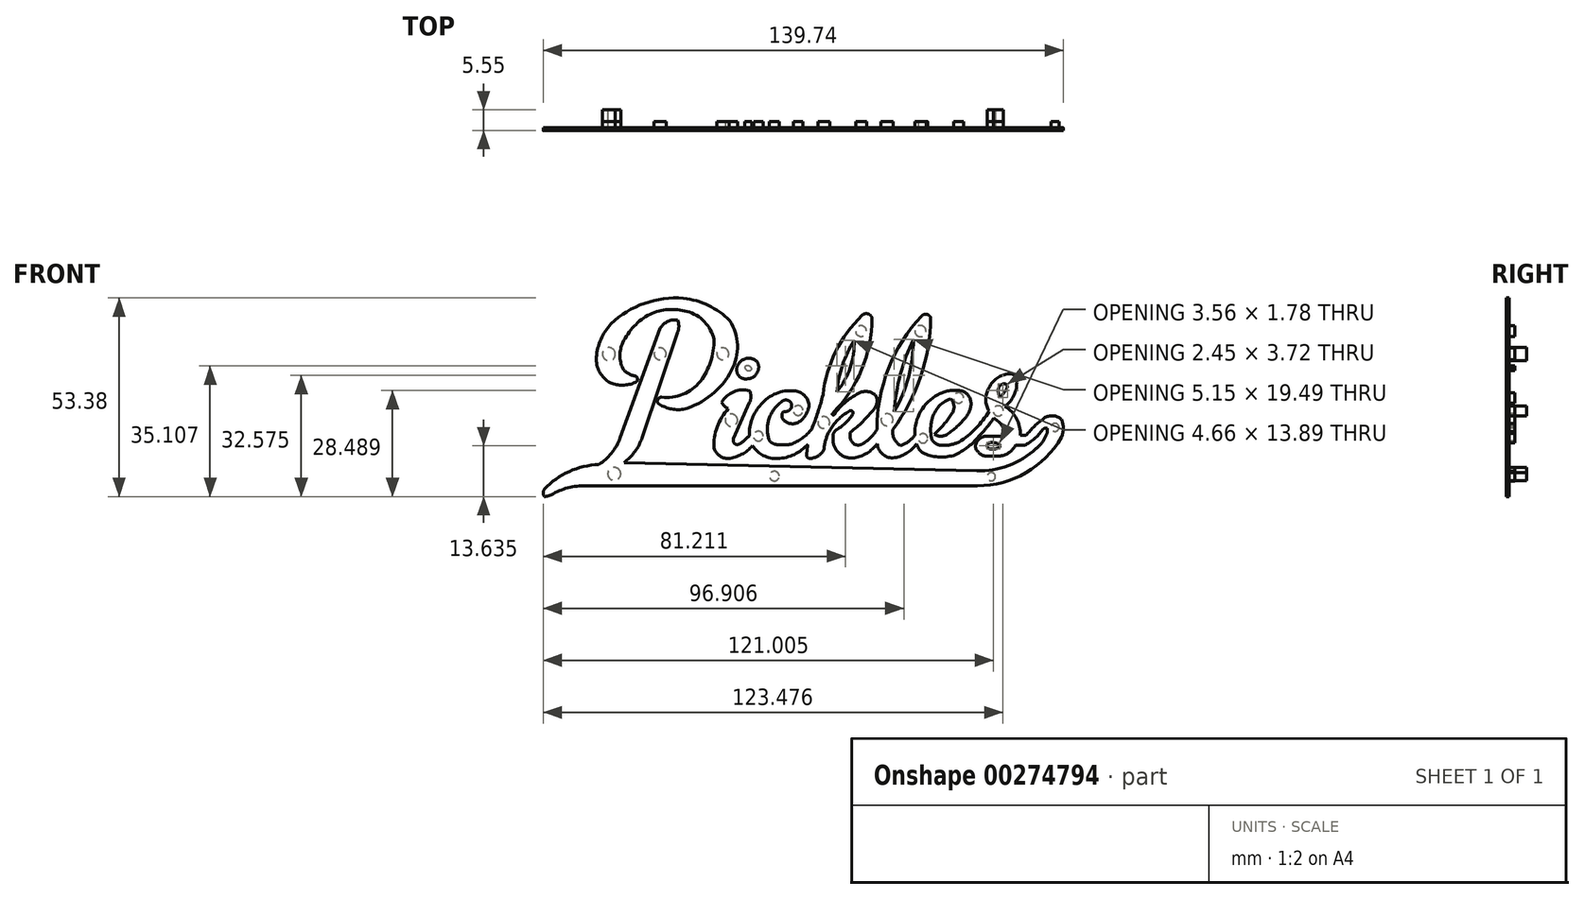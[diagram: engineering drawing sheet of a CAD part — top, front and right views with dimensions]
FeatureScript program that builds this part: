
annotation { "Feature Type Name" : "Feature", "Feature Type Description" : "" }
export const myFeature = defineFeature(function(context is Context, id is Id, definition is map)
    precondition{}
    {
        {
            var Q0;
            Q0=qCreatedBy(makeId("Front.planeOp"),FACE);
            var sketch = newSketch(context, id + "F0", { "sketchPlane" : qUnion([Q0])});
            skArc(sketch, "E0", {"start": v(-54.7, 9.9) * mm, "mid": v(-51.38, 9.32) * mm, "end": v(-48.08, 10.03) * mm});
            skArc(sketch, "E1", {"start": v(-58.51, 16.82) * mm, "mid": v(-57.6, 12.82) * mm, "end": v(-54.7, 9.9) * mm});
            skArc(sketch, "E2", {"start": v(-54.57, 25.8) * mm, "mid": v(-57.28, 21.63) * mm, "end": v(-58.51, 16.82) * mm});
            skArc(sketch, "E3", {"start": v(-35.11, 32.66) * mm, "mid": v(-45.57, 31.3) * mm, "end": v(-54.57, 25.8) * mm});
            skArc(sketch, "E4", {"start": v(-22.67, 26.65) * mm, "mid": v(-28.37, 30.74) * mm, "end": v(-35.11, 32.66) * mm});
            skArc(sketch, "E5", {"start": v(-22.17, 13.33) * mm, "mid": v(-20.58, 20.06) * mm, "end": v(-22.67, 26.65) * mm});
            skArc(sketch, "E6", {"start": v(-35.11, 2.8) * mm, "mid": v(-27.55, 6.72) * mm, "end": v(-22.17, 13.33) * mm});
            skArc(sketch, "E7", {"start": v(-41.96, 4.45) * mm, "mid": v(-38.7, 2.99) * mm, "end": v(-35.11, 2.8) * mm});
            skArc(sketch, "E8", {"start": v(-41.02, 6.1) * mm, "mid": v(-41.94, 5.53) * mm, "end": v(-41.96, 4.45) * mm});
            skArc(sketch, "E9", {"start": v(-41.02, 6.1) * mm, "mid": v(-35.23, 6.85) * mm, "end": v(-30.55, 10.33) * mm});
            skArc(sketch, "E10", {"start": v(-30.55, 10.33) * mm, "mid": v(-27.78, 15.65) * mm, "end": v(-26.9, 21.58) * mm});
            skArc(sketch, "E11", {"start": v(-26.9, 21.58) * mm, "mid": v(-29.46, 26.35) * mm, "end": v(-34.12, 29.13) * mm});
            skArc(sketch, "E12", {"start": v(-34.12, 29.13) * mm, "mid": v(-39.17, 29.63) * mm, "end": v(-44.1, 28.4) * mm});
            skArc(sketch, "E13", {"start": v(-44.1, 28.4) * mm, "mid": v(-48.36, 25.13) * mm, "end": v(-51.4, 20.71) * mm});
            skArc(sketch, "E14", {"start": v(-51.4, 20.71) * mm, "mid": v(-52.15, 17.27) * mm, "end": v(-51.4, 13.82) * mm});
            skArc(sketch, "E15", {"start": v(-51.4, 13.82) * mm, "mid": v(-49.9, 12.42) * mm, "end": v(-47.96, 11.76) * mm});
            skArc(sketch, "E16", {"start": v(-48.08, 10.03) * mm, "mid": v(-47.4, 10.85) * mm, "end": v(-47.96, 11.76) * mm});
            skArc(sketch, "E17", {"start": v(-36.65, 26.8) * mm, "mid": v(-39.31, 26.43) * mm, "end": v(-41.3, 24.63) * mm});
            skArc(sketch, "E18", {"start": v(-36.65, 23.5) * mm, "mid": v(-36.33, 25.15) * mm, "end": v(-36.65, 26.8) * mm});
            skLineSegment(sketch, "E19", {"start": v(-41.3, 24.63) * mm, "end": v(-52.12, -4.9) * mm});
            skLineSegment(sketch, "E20", {"start": v(-36.65, 23.5) * mm, "end": v(-46.17, -4.75) * mm});
            skArc(sketch, "E21", {"start": v(-51.06, -11.47) * mm, "mid": v(-48.1, -8.49) * mm, "end": v(-46.17, -4.75) * mm});
            skArc(sketch, "E22", {"start": v(-57.84, -12.05) * mm, "mid": v(-54.4, -8.95) * mm, "end": v(-52.12, -4.9) * mm});
            skArc(sketch, "E23", {"start": v(-57.84, -12.05) * mm, "mid": v(-65.8, -13.88) * mm, "end": v(-72.41, -18.66) * mm});
            skArc(sketch, "E24", {"start": v(-61.3, -17.73) * mm, "mid": v(-66.12, -18.3) * mm, "end": v(-70.6, -20.15) * mm});
            skArc(sketch, "E25", {"start": v(-72.41, -20.64) * mm, "mid": v(-71.49, -20.48) * mm, "end": v(-70.6, -20.15) * mm});
            skArc(sketch, "E26", {"start": v(-72.41, -18.66) * mm, "mid": v(-72.78, -19.65) * mm, "end": v(-72.41, -20.64) * mm});
            skLineSegment(sketch, "E27", {"start": v(-61.3, -17.73) * mm, "end": v(43.85, -17.73) * mm});
            skLineSegment(sketch, "E28", {"start": v(-51.06, -11.47) * mm, "end": v(43.72, -13.74) * mm});
            skArc(sketch, "E29", {"start": v(43.72, -13.74) * mm, "mid": v(52.27, -12.29) * mm, "end": v(59.66, -7.75) * mm});
            skArc(sketch, "E30", {"start": v(43.85, -17.73) * mm, "mid": v(56.9, -14.23) * mm, "end": v(66.45, -4.67) * mm});
            skArc(sketch, "E31", {"start": v(59.66, -7.75) * mm, "mid": v(61.3, -6.08) * mm, "end": v(62.43, -4.04) * mm});
            skArc(sketch, "E32", {"start": v(62.43, -4.04) * mm, "mid": v(62.67, -3.16) * mm, "end": v(62.69, -2.25) * mm});
            skArc(sketch, "E33", {"start": v(62.69, -2.25) * mm, "mid": v(61.98, -2.3) * mm, "end": v(61.38, -2.69) * mm});
            skArc(sketch, "E34", {"start": v(56.53, -6.87) * mm, "mid": v(59.22, -5.08) * mm, "end": v(61.38, -2.69) * mm});
            skLineSegment(sketch, "E35", {"start": v(56.53, -6.87) * mm, "end": v(54.08, -6.87) * mm});
            skArc(sketch, "E36", {"start": v(66.45, -4.67) * mm, "mid": v(66.96, -2.28) * mm, "end": v(66.45, 0.12) * mm});
            skArc(sketch, "E37", {"start": v(61.8, 0.47) * mm, "mid": v(59.22, -1.72) * mm, "end": v(56.95, -4.21) * mm});
            skArc(sketch, "E38", {"start": v(66.45, 0.12) * mm, "mid": v(64.18, 1.08) * mm, "end": v(61.8, 0.47) * mm});
            skLineSegment(sketch, "E39", {"start": v(56.95, -4.21) * mm, "end": v(55.36, -4.21) * mm});
            skArc(sketch, "E40", {"start": v(49.68, -9.75) * mm, "mid": v(52.27, -8.9) * mm, "end": v(54.08, -6.87) * mm});
            skLineSegment(sketch, "E41", {"start": v(49.68, -9.75) * mm, "end": v(46.47, -9.75) * mm});
            skArc(sketch, "E42", {"start": v(43.35, -7.37) * mm, "mid": v(44.5, -9.09) * mm, "end": v(46.47, -9.75) * mm});
            skArc(sketch, "E43", {"start": v(45.81, -4.46) * mm, "mid": v(44.06, -5.48) * mm, "end": v(43.35, -7.37) * mm});
            skLineSegment(sketch, "E44", {"start": v(45.81, -4.46) * mm, "end": v(51.38, -4.46) * mm});
            skArc(sketch, "E45", {"start": v(51.38, -4.46) * mm, "mid": v(50.5, -1.59) * mm, "end": v(48.25, 0.42) * mm});
            skArc(sketch, "E46", {"start": v(44.66, -4.02) * mm, "mid": v(46.55, -1.88) * mm, "end": v(48.25, 0.42) * mm});
            skArc(sketch, "E47", {"start": v(37.45, -9.59) * mm, "mid": v(41.4, -7.25) * mm, "end": v(44.66, -4.02) * mm});
            skArc(sketch, "E48", {"start": v(29.2, -8.89) * mm, "mid": v(33.27, -9.96) * mm, "end": v(37.45, -9.59) * mm});
            skArc(sketch, "E49", {"start": v(27.57, -6.47) * mm, "mid": v(28.15, -7.84) * mm, "end": v(29.2, -8.89) * mm});
            skArc(sketch, "E50", {"start": v(55.36, -4.21) * mm, "mid": v(54.42, 0.29) * mm, "end": v(51.25, 3.61) * mm});
            skArc(sketch, "E51", {"start": v(51.25, 3.61) * mm, "mid": v(53.88, 6.97) * mm, "end": v(54.36, 11.2) * mm});
            skArc(sketch, "E52", {"start": v(54.36, 11.2) * mm, "mid": v(53.55, 12.11) * mm, "end": v(52.36, 12.35) * mm});
            skArc(sketch, "E53", {"start": v(52.36, 12.35) * mm, "mid": v(49.2, 11.21) * mm, "end": v(47.04, 8.65) * mm});
            skArc(sketch, "E54", {"start": v(47.04, 8.65) * mm, "mid": v(46.15, 5.48) * mm, "end": v(47.04, 2.3) * mm});
            skArc(sketch, "E55", {"start": v(39, -5.95) * mm, "mid": v(43.48, -2.28) * mm, "end": v(47.04, 2.3) * mm});
            skArc(sketch, "E56", {"start": v(36.7, 5.63) * mm, "mid": v(33.26, 3.28) * mm, "end": v(31.53, -0.51) * mm});
            skArc(sketch, "E57", {"start": v(37.05, 1.64) * mm, "mid": v(37.6, 3.7) * mm, "end": v(36.7, 5.63) * mm});
            skArc(sketch, "E58", {"start": v(32.32, -3.88) * mm, "mid": v(34.86, -1.27) * mm, "end": v(37.05, 1.64) * mm});
            skArc(sketch, "E59", {"start": v(32.32, -3.88) * mm, "mid": v(34.03, -4.42) * mm, "end": v(35.73, -3.88) * mm});
            skArc(sketch, "E60", {"start": v(35.73, -3.88) * mm, "mid": v(38.45, -1.81) * mm, "end": v(40.77, 0.7) * mm});
            skArc(sketch, "E61", {"start": v(40.77, 0.7) * mm, "mid": v(41.76, 2.35) * mm, "end": v(42.16, 4.23) * mm});
            skArc(sketch, "E62", {"start": v(42.16, 4.23) * mm, "mid": v(41.45, 6.52) * mm, "end": v(39.42, 7.8) * mm});
            skArc(sketch, "E63", {"start": v(39.42, 7.8) * mm, "mid": v(36.29, 7.8) * mm, "end": v(33.33, 6.8) * mm});
            skArc(sketch, "E64", {"start": v(33.33, 6.8) * mm, "mid": v(28.64, 2.26) * mm, "end": v(27.1, -4.08) * mm});
            skArc(sketch, "E65", {"start": v(23.2, -6.91) * mm, "mid": v(25.38, -5.81) * mm, "end": v(27.1, -4.08) * mm});
            skArc(sketch, "E66", {"start": v(21.15, -2.6) * mm, "mid": v(21.5, -5.07) * mm, "end": v(23.2, -6.91) * mm});
            skArc(sketch, "E67", {"start": v(21.15, -2.6) * mm, "mid": v(28.64, 11.64) * mm, "end": v(31.33, 27.5) * mm});
            skArc(sketch, "E68", {"start": v(31.33, 27.5) * mm, "mid": v(30.2, 28.35) * mm, "end": v(28.85, 27.9) * mm});
            skArc(sketch, "E69", {"start": v(28.85, 27.9) * mm, "mid": v(19.98, 13.78) * mm, "end": v(16.93, -2.6) * mm});
            skArc(sketch, "E70", {"start": v(21.15, -10.26) * mm, "mid": v(24.76, -9.04) * mm, "end": v(27.57, -6.47) * mm});
            skArc(sketch, "E71", {"start": v(16.93, -6.47) * mm, "mid": v(18.33, -9.15) * mm, "end": v(21.15, -10.26) * mm});
            skArc(sketch, "E72", {"start": v(10.8, -10.26) * mm, "mid": v(14.22, -8.94) * mm, "end": v(16.93, -6.47) * mm});
            skArc(sketch, "E73", {"start": v(5.1, -4.74) * mm, "mid": v(6.61, -8.87) * mm, "end": v(10.8, -10.26) * mm});
            skArc(sketch, "E74", {"start": v(6.18, -2.6) * mm, "mid": v(5.3, -3.5) * mm, "end": v(5.1, -4.74) * mm});
            skArc(sketch, "E75", {"start": v(6.18, -2.6) * mm, "mid": v(8.55, -0.76) * mm, "end": v(10.45, 1.57) * mm});
            skArc(sketch, "E76", {"start": v(9.45, 2.36) * mm, "mid": v(6.38, -0.02) * mm, "end": v(4.05, -3.13) * mm});
            skArc(sketch, "E77", {"start": v(10.45, 1.57) * mm, "mid": v(10.23, 2.33) * mm, "end": v(9.45, 2.36) * mm});
            skArc(sketch, "E78", {"start": v(4.05, -3.13) * mm, "mid": v(3.08, -5.55) * mm, "end": v(2.62, -8.12) * mm});
            skArc(sketch, "E79", {"start": v(-1.14, -10.4) * mm, "mid": v(1.02, -9.72) * mm, "end": v(2.62, -8.12) * mm});
            skArc(sketch, "E80", {"start": v(-2.03, -9.47) * mm, "mid": v(-1.78, -10.12) * mm, "end": v(-1.14, -10.4) * mm});
            skArc(sketch, "E81", {"start": v(-1.66, -6.54) * mm, "mid": v(-1.86, -8) * mm, "end": v(-2.03, -9.47) * mm});
            skArc(sketch, "E82", {"start": v(-9.76, -10.4) * mm, "mid": v(-5.3, -9.31) * mm, "end": v(-1.66, -6.54) * mm});
            skArc(sketch, "E83", {"start": v(-16.54, -6.96) * mm, "mid": v(-13.62, -9.6) * mm, "end": v(-9.76, -10.4) * mm});
            skArc(sketch, "E84", {"start": v(-23.03, -10.4) * mm, "mid": v(-19.46, -9.3) * mm, "end": v(-16.54, -6.96) * mm});
            skArc(sketch, "E85", {"start": v(-26.84, -7.62) * mm, "mid": v(-25.42, -9.68) * mm, "end": v(-23.03, -10.4) * mm});
            skArc(sketch, "E86", {"start": v(-23.03, 3.02) * mm, "mid": v(-26.05, -1.9) * mm, "end": v(-26.84, -7.62) * mm});
            skArc(sketch, "E87", {"start": v(-24.83, 4.7) * mm, "mid": v(-24.09, 3.69) * mm, "end": v(-23.03, 3.02) * mm});
            skArc(sketch, "E88", {"start": v(-17.32, 7.82) * mm, "mid": v(-21.6, 7.53) * mm, "end": v(-24.83, 4.7) * mm});
            skArc(sketch, "E89", {"start": v(-17.32, 4.7) * mm, "mid": v(-16.97, 6.26) * mm, "end": v(-17.32, 7.82) * mm});
            skLineSegment(sketch, "E90", {"start": v(-17.32, 4.7) * mm, "end": v(-21.64, -5.1) * mm});
            skArc(sketch, "E91", {"start": v(-21.64, -5.1) * mm, "mid": v(-21.3, -6.44) * mm, "end": v(-19.9, -6.4) * mm});
            skArc(sketch, "E92", {"start": v(-19.9, -6.4) * mm, "mid": v(-18.59, -5.38) * mm, "end": v(-17.38, -4.24) * mm});
            skArc(sketch, "E93", {"start": v(-14.2, 4.17) * mm, "mid": v(-16.63, 0.28) * mm, "end": v(-17.38, -4.24) * mm});
            skArc(sketch, "E94", {"start": v(-5.33, 7.78) * mm, "mid": v(-10.2, 7.07) * mm, "end": v(-14.2, 4.17) * mm});
            skArc(sketch, "E95", {"start": v(-1.33, 3.86) * mm, "mid": v(-2.6, 6.57) * mm, "end": v(-5.33, 7.78) * mm});
            skArc(sketch, "E96", {"start": v(-4.28, -0.71) * mm, "mid": v(-2.3, 1.24) * mm, "end": v(-1.33, 3.86) * mm});
            skArc(sketch, "E97", {"start": v(-8.27, 0.02) * mm, "mid": v(-6.4, -1) * mm, "end": v(-4.28, -0.71) * mm});
            skArc(sketch, "E98", {"start": v(-8.27, 2.23) * mm, "mid": v(-8.62, 1.13) * mm, "end": v(-8.27, 0.02) * mm});
            skArc(sketch, "E99", {"start": v(-8.27, 2.23) * mm, "mid": v(-7.13, 2.31) * mm, "end": v(-6.22, 3) * mm});
            skArc(sketch, "E100", {"start": v(-6.22, 3) * mm, "mid": v(-6.1, 4.35) * mm, "end": v(-7.1, 5.26) * mm});
            skArc(sketch, "E101", {"start": v(-7.1, 5.26) * mm, "mid": v(-7.87, 5.3) * mm, "end": v(-8.6, 5.02) * mm});
            skArc(sketch, "E102", {"start": v(-8.6, 5.02) * mm, "mid": v(-10.73, 2.84) * mm, "end": v(-12.18, 0.16) * mm});
            skArc(sketch, "E103", {"start": v(-12.18, 0.16) * mm, "mid": v(-12.52, -2.51) * mm, "end": v(-12.18, -5.18) * mm});
            skArc(sketch, "E104", {"start": v(-12.18, -5.18) * mm, "mid": v(-11.5, -6.08) * mm, "end": v(-10.5, -6.56) * mm});
            skArc(sketch, "E105", {"start": v(-10.5, -6.56) * mm, "mid": v(-8.37, -6.75) * mm, "end": v(-6.24, -6.56) * mm});
            skArc(sketch, "E106", {"start": v(-6.24, -6.56) * mm, "mid": v(-3.17, -4.93) * mm, "end": v(-0.66, -2.53) * mm});
            skArc(sketch, "E107", {"start": v(-0.66, -2.53) * mm, "mid": v(1.04, 2.05) * mm, "end": v(2.4, 6.75) * mm});
            skArc(sketch, "E108", {"start": v(12.88, 28.08) * mm, "mid": v(5.8, 18.31) * mm, "end": v(2.4, 6.75) * mm});
            skArc(sketch, "E109", {"start": v(15.58, 27.28) * mm, "mid": v(14.47, 28.49) * mm, "end": v(12.88, 28.08) * mm});
            skArc(sketch, "E110", {"start": v(4.96, 1.73) * mm, "mid": v(12.77, 13.46) * mm, "end": v(15.58, 27.28) * mm});
            skArc(sketch, "E111", {"start": v(4.96, 1.73) * mm, "mid": v(5.03, 1.28) * mm, "end": v(5.46, 1.46) * mm});
            skArc(sketch, "E112", {"start": v(12.44, 7.37) * mm, "mid": v(8.56, 4.87) * mm, "end": v(5.46, 1.46) * mm});
            skArc(sketch, "E113", {"start": v(16.37, 6.75) * mm, "mid": v(14.49, 7.58) * mm, "end": v(12.44, 7.37) * mm});
            skArc(sketch, "E114", {"start": v(16.16, 2.92) * mm, "mid": v(16.93, 4.8) * mm, "end": v(16.37, 6.75) * mm});
            skArc(sketch, "E115", {"start": v(9.73, -3.38) * mm, "mid": v(13.14, -0.43) * mm, "end": v(16.16, 2.92) * mm});
            skArc(sketch, "E116", {"start": v(9.73, -3.38) * mm, "mid": v(9.8, -5.12) * mm, "end": v(10.8, -6.56) * mm});
            skArc(sketch, "E117", {"start": v(10.8, -6.56) * mm, "mid": v(11.85, -6.8) * mm, "end": v(12.9, -6.56) * mm});
            skArc(sketch, "E118", {"start": v(12.9, -6.56) * mm, "mid": v(15.14, -4.81) * mm, "end": v(16.93, -2.6) * mm});
            skArc(sketch, "E119", {"start": v(31.53, -0.51) * mm, "mid": v(31.33, -2.7) * mm, "end": v(31.53, -4.9) * mm});
            skArc(sketch, "E120", {"start": v(31.53, -4.9) * mm, "mid": v(32.64, -6.36) * mm, "end": v(34.4, -6.82) * mm});
            skArc(sketch, "E121", {"start": v(34.4, -6.82) * mm, "mid": v(36.76, -6.68) * mm, "end": v(39, -5.95) * mm});
            skArc(sketch, "E122", {"start": v(47.11, -6.16) * mm, "mid": v(46.45, -6.92) * mm, "end": v(47.03, -7.75) * mm});
            skArc(sketch, "E123", {"start": v(47.03, -7.75) * mm, "mid": v(48.45, -7.87) * mm, "end": v(49.8, -7.42) * mm});
            skArc(sketch, "E124", {"start": v(49.8, -7.42) * mm, "mid": v(49.99, -6.84) * mm, "end": v(49.55, -6.41) * mm});
            skArc(sketch, "E125", {"start": v(49.55, -6.41) * mm, "mid": v(48.35, -6.14) * mm, "end": v(47.11, -6.16) * mm});
            skArc(sketch, "E126", {"start": v(51.46, 9.68) * mm, "mid": v(50.28, 9.47) * mm, "end": v(49.55, 8.51) * mm});
            skArc(sketch, "E127", {"start": v(49.55, 8.51) * mm, "mid": v(49.51, 7.2) * mm, "end": v(49.96, 5.99) * mm});
            skArc(sketch, "E128", {"start": v(51.88, 8.58) * mm, "mid": v(51.86, 9.2) * mm, "end": v(51.46, 9.68) * mm});
            skArc(sketch, "E129", {"start": v(49.96, 5.99) * mm, "mid": v(51, 7.22) * mm, "end": v(51.88, 8.58) * mm});
            skArc(sketch, "E130", {"start": v(26.7, 21.68) * mm, "mid": v(23.16, 12.19) * mm, "end": v(21.55, 2.2) * mm});
            skArc(sketch, "E131", {"start": v(21.55, 2.2) * mm, "mid": v(25.4, 11.6) * mm, "end": v(26.7, 21.68) * mm});
            skArc(sketch, "E132", {"start": v(10.76, 21.41) * mm, "mid": v(7.67, 14.72) * mm, "end": v(6.1, 7.52) * mm});
            skArc(sketch, "E133", {"start": v(6.1, 7.52) * mm, "mid": v(9.7, 14.04) * mm, "end": v(10.76, 21.41) * mm});
            skArc(sketch, "E134", {"start": v(-15.35, 15.68) * mm, "mid": v(-18.4, 16.43) * mm, "end": v(-20.67, 14.26) * mm});
            skArc(sketch, "E135", {"start": v(-20.67, 14.26) * mm, "mid": v(-20.2, 11.84) * mm, "end": v(-17.88, 11.01) * mm});
            skArc(sketch, "E136", {"start": v(-17.88, 11.01) * mm, "mid": v(-16.18, 11.58) * mm, "end": v(-15.13, 13.04) * mm});
            skArc(sketch, "E137", {"start": v(-15.13, 13.04) * mm, "mid": v(-14.88, 14.39) * mm, "end": v(-15.35, 15.68) * mm});
            skCircle(sketch, "E138", {"center": v(-55.08, 17.68) * mm, "radius": 1.73 * mm});
            skCircle(sketch, "E139", {"center": v(-41.33, 17.73) * mm, "radius": 1.62 * mm});
            skCircle(sketch, "E140", {"center": v(-24.49, 17.73) * mm, "radius": 1.62 * mm});
            skCircle(sketch, "E141", {"center": v(-53.67, -14.55) * mm, "radius": 1.73 * mm});
            skCircle(sketch, "E142", {"center": v(-22.17, -0.12) * mm, "radius": 1.66 * mm});
            skCircle(sketch, "E143", {"center": v(-14.94, -4.37) * mm, "radius": 1.31 * mm});
            skCircle(sketch, "E144", {"center": v(-10.66, -15.13) * mm, "radius": 1.3 * mm});
            skCircle(sketch, "E145", {"center": v(-4.28, 2.52) * mm, "radius": 1.31 * mm});
            skCircle(sketch, "E146", {"center": v(2.62, -0.71) * mm, "radius": 1.6 * mm});
            skCircle(sketch, "E147", {"center": v(12.63, 23.86) * mm, "radius": 1.46 * mm});
            skCircle(sketch, "E148", {"center": v(28.6, 23.86) * mm, "radius": 1.5 * mm});
            skCircle(sketch, "E149", {"center": v(19.62, 0.03) * mm, "radius": 1.61 * mm});
            skCircle(sketch, "E150", {"center": v(29.28, -4.97) * mm, "radius": 1.27 * mm});
            skCircle(sketch, "E151", {"center": v(38.84, 5.89) * mm, "radius": 1.38 * mm});
            skCircle(sketch, "E152", {"center": v(49.5, 2.4) * mm, "radius": 1.37 * mm});
            skCircle(sketch, "E153", {"center": v(47.64, -15.28) * mm, "radius": 1.1 * mm});
            skCircle(sketch, "E154", {"center": v(64.74, -2.04) * mm, "radius": 1.09 * mm});
            skArc(sketch, "E155", {"start": v(-16.67, 13.63) * mm, "mid": v(-17.5, 14.47) * mm, "end": v(-18.64, 14.21) * mm});
            skArc(sketch, "E156", {"start": v(-18.64, 14.21) * mm, "mid": v(-17.86, 13.26) * mm, "end": v(-16.67, 13.63) * mm});
            skSolve(sketch);
        }
        {
            var Q0;
            Q0=makeQuery(id+"F0.imprint","IMPRINT",FACE,{"disambiguationData":[TD([[makeQuery(id+"F0.imprint","IMPRINT",EDGE,{"derivedFrom":sQuery(id+"F0.wireOp",EDGE,"E17")}),1.0]])]});
            var Q1;
            Q1=makeQuery(id+"F0.imprint","IMPRINT",FACE,{"disambiguationData":[TD([[makeQuery(id+"F0.imprint","IMPRINT",EDGE,{"derivedFrom":sQuery(id+"F0.wireOp",EDGE,"E134")}),1.0]])]});
            var Q2;
            Q2=makeQuery(id+"F0.imprint","IMPRINT",FACE,{"disambiguationData":[TD([[makeQuery(id+"F0.imprint","IMPRINT",EDGE,{"derivedFrom":sQuery(id+"F0.wireOp",EDGE,"E0")}),1.0]])]});
            var Q3;
            Q3=makeQuery(id+"F0.imprint","IMPRINT",FACE,{"disambiguationData":[TD([[makeQuery(id+"F0.imprint","IMPRINT",EDGE,{"derivedFrom":sQuery(id+"F0.wireOp",EDGE,"E141")}),1.0]])]});
            var Q4;
            Q4=makeQuery(id+"F0.imprint","IMPRINT",FACE,{"disambiguationData":[TD([[makeQuery(id+"F0.imprint","IMPRINT",EDGE,{"derivedFrom":sQuery(id+"F0.wireOp",EDGE,"E144")}),1.0]])]});
            var Q5;
            Q5=makeQuery(id+"F0.imprint","IMPRINT",FACE,{"disambiguationData":[TD([[makeQuery(id+"F0.imprint","IMPRINT",EDGE,{"derivedFrom":sQuery(id+"F0.wireOp",EDGE,"E153")}),1.0]])]});
            var Q6;
            Q6=makeQuery(id+"F0.imprint","IMPRINT",FACE,{"disambiguationData":[TD([[makeQuery(id+"F0.imprint","IMPRINT",EDGE,{"derivedFrom":sQuery(id+"F0.wireOp",EDGE,"E154")}),1.0]])]});
            var Q7;
            Q7=makeQuery(id+"F0.imprint","IMPRINT",FACE,{"disambiguationData":[TD([[makeQuery(id+"F0.imprint","IMPRINT",EDGE,{"derivedFrom":sQuery(id+"F0.wireOp",EDGE,"E152")}),1.0]])]});
            var Q8;
            Q8=makeQuery(id+"F0.imprint","IMPRINT",FACE,{"disambiguationData":[TD([[makeQuery(id+"F0.imprint","IMPRINT",EDGE,{"derivedFrom":sQuery(id+"F0.wireOp",EDGE,"E151")}),1.0]])]});
            var Q9;
            Q9=makeQuery(id+"F0.imprint","IMPRINT",FACE,{"disambiguationData":[TD([[makeQuery(id+"F0.imprint","IMPRINT",EDGE,{"derivedFrom":sQuery(id+"F0.wireOp",EDGE,"E150")}),1.0]])]});
            var Q10;
            Q10=makeQuery(id+"F0.imprint","IMPRINT",FACE,{"disambiguationData":[TD([[makeQuery(id+"F0.imprint","IMPRINT",EDGE,{"derivedFrom":sQuery(id+"F0.wireOp",EDGE,"E149")}),1.0]])]});
            var Q11;
            Q11=makeQuery(id+"F0.imprint","IMPRINT",FACE,{"disambiguationData":[TD([[makeQuery(id+"F0.imprint","IMPRINT",EDGE,{"derivedFrom":sQuery(id+"F0.wireOp",EDGE,"E146")}),1.0]])]});
            var Q12;
            Q12=makeQuery(id+"F0.imprint","IMPRINT",FACE,{"disambiguationData":[TD([[makeQuery(id+"F0.imprint","IMPRINT",EDGE,{"derivedFrom":sQuery(id+"F0.wireOp",EDGE,"E148")}),1.0]])]});
            var Q13;
            Q13=makeQuery(id+"F0.imprint","IMPRINT",FACE,{"disambiguationData":[TD([[makeQuery(id+"F0.imprint","IMPRINT",EDGE,{"derivedFrom":sQuery(id+"F0.wireOp",EDGE,"E145")}),1.0]])]});
            var Q14;
            Q14=makeQuery(id+"F0.imprint","IMPRINT",FACE,{"disambiguationData":[TD([[makeQuery(id+"F0.imprint","IMPRINT",EDGE,{"derivedFrom":sQuery(id+"F0.wireOp",EDGE,"E143")}),1.0]])]});
            var Q15;
            Q15=makeQuery(id+"F0.imprint","IMPRINT",FACE,{"disambiguationData":[TD([[makeQuery(id+"F0.imprint","IMPRINT",EDGE,{"derivedFrom":sQuery(id+"F0.wireOp",EDGE,"E142")}),1.0]])]});
            var Q16;
            Q16=makeQuery(id+"F0.imprint","IMPRINT",FACE,{"disambiguationData":[TD([[makeQuery(id+"F0.imprint","IMPRINT",EDGE,{"derivedFrom":sQuery(id+"F0.wireOp",EDGE,"E155")}),1.0]])]});
            var Q17;
            Q17=makeQuery(id+"F0.imprint","IMPRINT",FACE,{"disambiguationData":[TD([[makeQuery(id+"F0.imprint","IMPRINT",EDGE,{"derivedFrom":sQuery(id+"F0.wireOp",EDGE,"E140")}),1.0]])]});
            var Q18;
            Q18=makeQuery(id+"F0.imprint","IMPRINT",FACE,{"disambiguationData":[TD([[makeQuery(id+"F0.imprint","IMPRINT",EDGE,{"derivedFrom":sQuery(id+"F0.wireOp",EDGE,"E139")}),1.0]])]});
            var Q19;
            Q19=makeQuery(id+"F0.imprint","IMPRINT",FACE,{"disambiguationData":[TD([[makeQuery(id+"F0.imprint","IMPRINT",EDGE,{"derivedFrom":sQuery(id+"F0.wireOp",EDGE,"E138")}),1.0]])]});
            var Q20;
            Q20=makeQuery(id+"F0.imprint","IMPRINT",FACE,{"disambiguationData":[TD([[makeQuery(id+"F0.imprint","IMPRINT",EDGE,{"derivedFrom":sQuery(id+"F0.wireOp",EDGE,"E147")}),1.0]])]});
            extrude(context, id + "F1", {"entities" : qUnion([Q0, Q1, Q2, Q3, Q4, Q5, Q6, Q7, Q8, Q9, Q10, Q11, Q12, Q13, Q14, Q15, Q16, Q17, Q18, Q19, Q20]), "depth" : 0.8 * mm});
        }
        {
            var Q0;
            Q0=qCreatedBy(makeId("Front.planeOp"),FACE);
            var sketch = newSketch(context, id + "F2", { "sketchPlane" : qUnion([Q0])});
            skCircle(sketch, "E157", {"center": v(-55.1, 17.67) * mm, "radius": 1.73 * mm});
            skCircle(sketch, "E158", {"center": v(-41.35, 17.72) * mm, "radius": 1.62 * mm});
            skCircle(sketch, "E159", {"center": v(-24.5, 17.72) * mm, "radius": 1.62 * mm});
            skCircle(sketch, "E160", {"center": v(-53.69, -14.56) * mm, "radius": 1.73 * mm});
            skCircle(sketch, "E161", {"center": v(-22.2, -0.13) * mm, "radius": 1.66 * mm});
            skCircle(sketch, "E162", {"center": v(-14.96, -4.38) * mm, "radius": 1.31 * mm});
            skCircle(sketch, "E163", {"center": v(-10.68, -15.13) * mm, "radius": 1.3 * mm});
            skCircle(sketch, "E164", {"center": v(-4.3, 2.51) * mm, "radius": 1.31 * mm});
            skCircle(sketch, "E165", {"center": v(2.6, -0.72) * mm, "radius": 1.6 * mm});
            skCircle(sketch, "E166", {"center": v(12.61, 23.85) * mm, "radius": 1.46 * mm});
            skCircle(sketch, "E167", {"center": v(28.58, 23.85) * mm, "radius": 1.5 * mm});
            skCircle(sketch, "E168", {"center": v(19.6, 0.02) * mm, "radius": 1.61 * mm});
            skCircle(sketch, "E169", {"center": v(29.26, -4.97) * mm, "radius": 1.27 * mm});
            skCircle(sketch, "E170", {"center": v(38.82, 5.88) * mm, "radius": 1.38 * mm});
            skCircle(sketch, "E171", {"center": v(49.48, 2.4) * mm, "radius": 1.37 * mm});
            skCircle(sketch, "E172", {"center": v(47.63, -15.29) * mm, "radius": 1.1 * mm});
            skCircle(sketch, "E173", {"center": v(64.72, -2.04) * mm, "radius": 1.09 * mm});
            skArc(sketch, "E174", {"start": v(-16.7, 13.62) * mm, "mid": v(-17.51, 14.47) * mm, "end": v(-18.66, 14.2) * mm});
            skArc(sketch, "E175", {"start": v(-18.66, 14.2) * mm, "mid": v(-17.87, 13.26) * mm, "end": v(-16.7, 13.62) * mm});
            skSolve(sketch);
        }
        {
            var Q0;
            Q0=makeQuery(id+"F2.imprint","IMPRINT",FACE,{"disambiguationData":[TD([[makeQuery(id+"F2.imprint","IMPRINT",EDGE,{"derivedFrom":sQuery(id+"F2.wireOp",EDGE,"E173")}),1.0]])]});
            var Q1;
            Q1=makeQuery(id+"F2.imprint","IMPRINT",FACE,{"disambiguationData":[TD([[makeQuery(id+"F2.imprint","IMPRINT",EDGE,{"derivedFrom":sQuery(id+"F2.wireOp",EDGE,"E172")}),1.0]])]});
            var Q2;
            Q2=makeQuery(id+"F2.imprint","IMPRINT",FACE,{"disambiguationData":[TD([[makeQuery(id+"F2.imprint","IMPRINT",EDGE,{"derivedFrom":sQuery(id+"F2.wireOp",EDGE,"E171")}),1.0]])]});
            var Q3;
            Q3=makeQuery(id+"F2.imprint","IMPRINT",FACE,{"disambiguationData":[TD([[makeQuery(id+"F2.imprint","IMPRINT",EDGE,{"derivedFrom":sQuery(id+"F2.wireOp",EDGE,"E170")}),1.0]])]});
            var Q4;
            Q4=makeQuery(id+"F2.imprint","IMPRINT",FACE,{"disambiguationData":[TD([[makeQuery(id+"F2.imprint","IMPRINT",EDGE,{"derivedFrom":sQuery(id+"F2.wireOp",EDGE,"E169")}),1.0]])]});
            var Q5;
            Q5=makeQuery(id+"F2.imprint","IMPRINT",FACE,{"disambiguationData":[TD([[makeQuery(id+"F2.imprint","IMPRINT",EDGE,{"derivedFrom":sQuery(id+"F2.wireOp",EDGE,"E168")}),1.0]])]});
            var Q6;
            Q6=makeQuery(id+"F2.imprint","IMPRINT",FACE,{"disambiguationData":[TD([[makeQuery(id+"F2.imprint","IMPRINT",EDGE,{"derivedFrom":sQuery(id+"F2.wireOp",EDGE,"E167")}),1.0]])]});
            var Q7;
            Q7=makeQuery(id+"F2.imprint","IMPRINT",FACE,{"disambiguationData":[TD([[makeQuery(id+"F2.imprint","IMPRINT",EDGE,{"derivedFrom":sQuery(id+"F2.wireOp",EDGE,"E166")}),1.0]])]});
            var Q8;
            Q8=makeQuery(id+"F2.imprint","IMPRINT",FACE,{"disambiguationData":[TD([[makeQuery(id+"F2.imprint","IMPRINT",EDGE,{"derivedFrom":sQuery(id+"F2.wireOp",EDGE,"E165")}),1.0]])]});
            var Q9;
            Q9=makeQuery(id+"F2.imprint","IMPRINT",FACE,{"disambiguationData":[TD([[makeQuery(id+"F2.imprint","IMPRINT",EDGE,{"derivedFrom":sQuery(id+"F2.wireOp",EDGE,"E164")}),1.0]])]});
            var Q10;
            Q10=makeQuery(id+"F2.imprint","IMPRINT",FACE,{"disambiguationData":[TD([[makeQuery(id+"F2.imprint","IMPRINT",EDGE,{"derivedFrom":sQuery(id+"F2.wireOp",EDGE,"E163")}),1.0]])]});
            var Q11;
            Q11=makeQuery(id+"F2.imprint","IMPRINT",FACE,{"disambiguationData":[TD([[makeQuery(id+"F2.imprint","IMPRINT",EDGE,{"derivedFrom":sQuery(id+"F2.wireOp",EDGE,"E162")}),1.0]])]});
            var Q12;
            Q12=makeQuery(id+"F2.imprint","IMPRINT",FACE,{"disambiguationData":[TD([[makeQuery(id+"F2.imprint","IMPRINT",EDGE,{"derivedFrom":sQuery(id+"F2.wireOp",EDGE,"E161")}),1.0]])]});
            var Q13;
            Q13=makeQuery(id+"F2.imprint","IMPRINT",FACE,{"disambiguationData":[TD([[makeQuery(id+"F2.imprint","IMPRINT",EDGE,{"derivedFrom":sQuery(id+"F2.wireOp",EDGE,"E174")}),1.0]])]});
            var Q14;
            Q14=makeQuery(id+"F2.imprint","IMPRINT",FACE,{"disambiguationData":[TD([[makeQuery(id+"F2.imprint","IMPRINT",EDGE,{"derivedFrom":sQuery(id+"F2.wireOp",EDGE,"E159")}),1.0]])]});
            var Q15;
            Q15=makeQuery(id+"F2.imprint","IMPRINT",FACE,{"disambiguationData":[TD([[makeQuery(id+"F2.imprint","IMPRINT",EDGE,{"derivedFrom":sQuery(id+"F2.wireOp",EDGE,"E158")}),1.0]])]});
            var Q16;
            Q16=makeQuery(id+"F2.imprint","IMPRINT",FACE,{"disambiguationData":[TD([[makeQuery(id+"F2.imprint","IMPRINT",EDGE,{"derivedFrom":sQuery(id+"F2.wireOp",EDGE,"E157")}),1.0]])]});
            var Q17;
            Q17=makeQuery(id+"F2.imprint","IMPRINT",FACE,{"disambiguationData":[TD([[makeQuery(id+"F2.imprint","IMPRINT",EDGE,{"derivedFrom":sQuery(id+"F2.wireOp",EDGE,"E160")}),1.0]])]});
            extrude(context, id + "F3", {"entities" : qUnion([Q0, Q1, Q2, Q3, Q4, Q5, Q6, Q7, Q8, Q9, Q10, Q11, Q12, Q13, Q14, Q15, Q16, Q17]), "oppositeDirection" : true, "offsetDistance" : 25.4 * mm, "depth" : 1.59 * mm});
        }
        {
            var Q0;
            Q0=makeQuery(id+"F3.opExtrude","CAP_FACE",FACE,{"disambiguationData":[OSD([sQuery(id+"F2.wireOp",EDGE,"E171")])],"isStart":false});
            var Q1;
            Q1=makeQuery(id+"F3.opExtrude","CAP_FACE",FACE,{"disambiguationData":[OSD([sQuery(id+"F2.wireOp",EDGE,"E172")])],"isStart":false});
            var Q2;
            Q2=makeQuery(id+"F3.opExtrude","CAP_FACE",FACE,{"disambiguationData":[OSD([sQuery(id+"F2.wireOp",EDGE,"E160")])],"isStart":false});
            var Q3;
            Q3=makeQuery(id+"F3.opExtrude","CAP_FACE",FACE,{"disambiguationData":[OSD([sQuery(id+"F2.wireOp",EDGE,"E157")])],"isStart":false});
            extrude(context, id + "F4", {"entities" : qUnion([Q0, Q1, Q2, Q3]), "offsetDistance" : 25.4 * mm, "depth" : 3.17 * mm});
        }
    });
